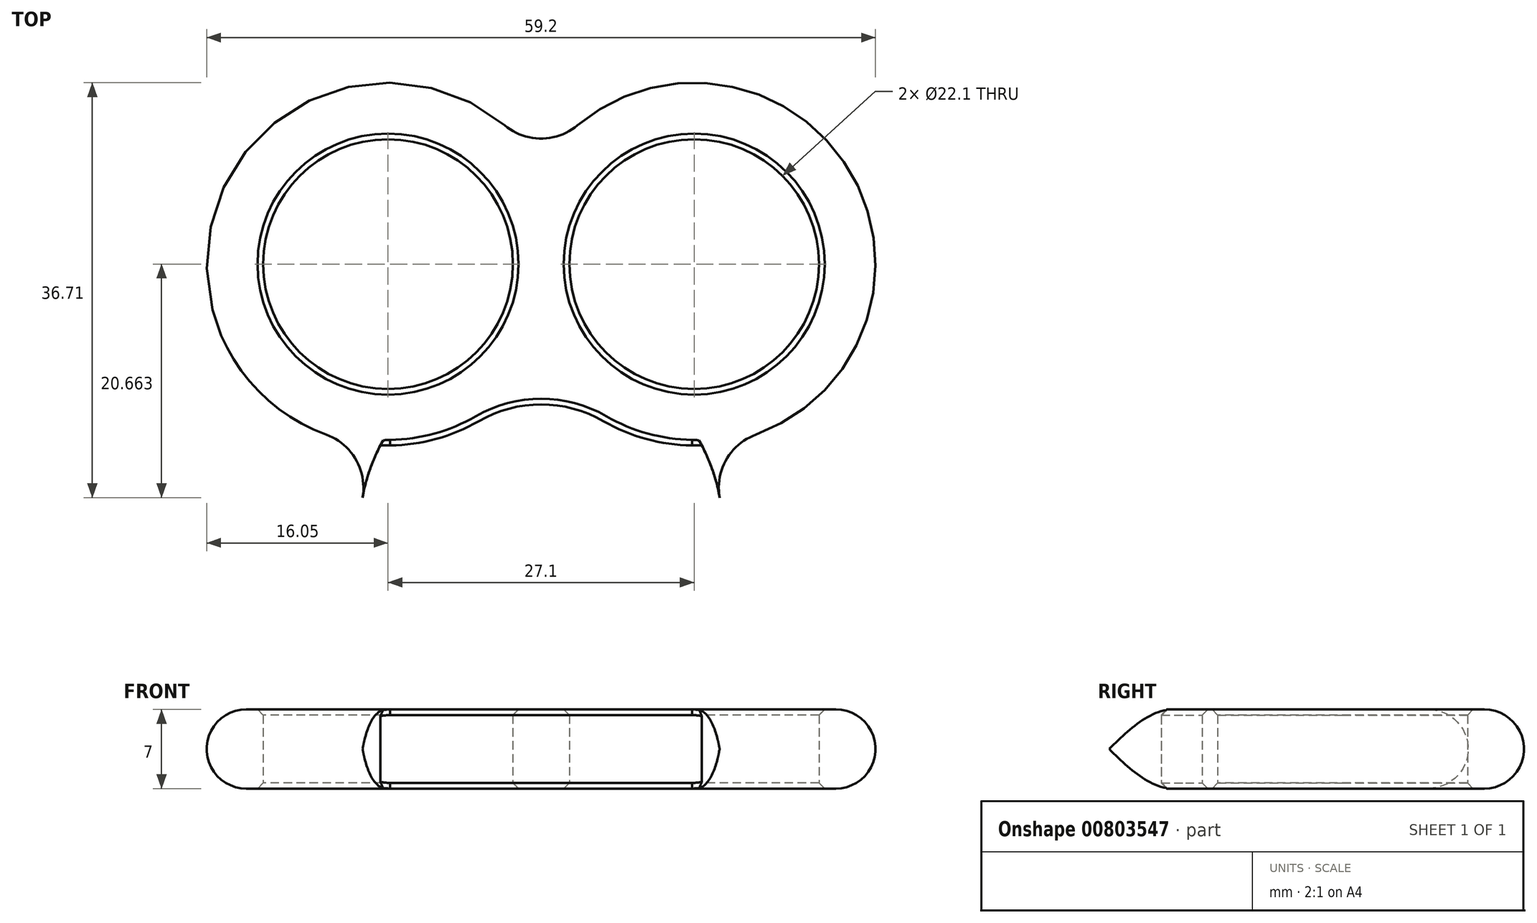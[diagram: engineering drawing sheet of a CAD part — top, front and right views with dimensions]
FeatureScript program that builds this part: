
annotation { "Feature Type Name" : "Feature", "Feature Type Description" : "" }
export const myFeature = defineFeature(function(context is Context, id is Id, definition is map)
    precondition{}
    {
        {
            var Q0;
            Q0=qCreatedBy(makeId("Top.planeOp"),FACE);
            var sketch = newSketch(context, id + "F0", { "sketchPlane" : qUnion([Q0])});
            skCircle(sketch, "E0", {"center": v(-13.55, 7.82) * mm, "radius": 11.05 * mm});
            skCircle(sketch, "E1", {"center": v(13.55, 7.82) * mm, "radius": 11.05 * mm});
            skCircle(sketch, "E2", {"center": v(0, -15.65) * mm, "radius": 11.05 * mm});
            skLineSegment(sketch, "E3", {"start": v(-13.55, 7.82) * mm, "end": v(13.55, 7.82) * mm, "construction": true});
            skLineSegment(sketch, "E4", {"start": v(13.55, 7.82) * mm, "end": v(0, -15.65) * mm, "construction": true});
            skLineSegment(sketch, "E5", {"start": v(0, -15.65) * mm, "end": v(-13.55, 7.82) * mm, "construction": true});
            skLineSegment(sketch, "E6", {"start": v(6.77, -3.91) * mm, "end": v(-13.55, 7.82) * mm, "construction": true});
            skArc(sketch, "E7", {"start": v(-3.22, 20.1) * mm, "mid": v(-27.45, 15.85) * mm, "end": v(-19.02, -7.27) * mm});
            skArc(sketch, "E8", {"start": v(19.02, -7.27) * mm, "mid": v(27.45, 15.85) * mm, "end": v(3.22, 20.1) * mm});
            skArc(sketch, "E9", {"start": v(-0.67, 0.39) * mm, "mid": v(0, -31.7) * mm, "end": v(0.67, 0.39) * mm});
            skArc(sketch, "E10.trimOffspring", {"start": v(0, -0.78) * mm, "mid": v(27.45, 15.85) * mm, "end": v(-0.67, 0.39) * mm});
            skArc(sketch, "E11.trimOffspring", {"start": v(-15.8, -12.84) * mm, "mid": v(0, -31.7) * mm, "end": v(15.8, -12.84) * mm});
            skArc(sketch, "E12.trimOffspring", {"start": v(0.67, 0.39) * mm, "mid": v(-27.45, 15.85) * mm, "end": v(0, -0.78) * mm});
            skPoint(sketch, "E13.visualSharp", {"position": v(0, 16.43) * mm});
            skArc(sketch, "E13.filletArc", {"start": v(-3.22, 20.1) * mm, "mid": v(0, 18.93) * mm, "end": v(3.22, 20.1) * mm});
            skPoint(sketch, "E14.visualSharp", {"position": v(14.22, -8.21) * mm});
            skArc(sketch, "E14.filletArc", {"start": v(19.02, -7.27) * mm, "mid": v(16.4, -9.47) * mm, "end": v(15.8, -12.84) * mm});
            skPoint(sketch, "E15.visualSharp", {"position": v(-14.22, -8.21) * mm});
            skArc(sketch, "E15.filletArc", {"start": v(-15.8, -12.84) * mm, "mid": v(-16.4, -9.47) * mm, "end": v(-19.02, -7.27) * mm});
            skSolve(sketch);
        }
        {
            var Q0;
            Q0=makeQuery(id+"F0.imprint","IMPRINT",FACE,{"disambiguationData":[TD([[makeQuery(id+"F0.imprint","IMPRINT",EDGE,{"derivedFrom":sQuery(id+"F0.wireOp",EDGE,"E0")}),-1.0]])]});
            var Q1;
            {var subQ4=sQuery(id+"F0.wireOp",EDGE,"E9");var subQ5=sQuery(id+"F0.wireOp",EDGE,"E0");var subQ6=makeQuery(id+"F0.imprint","INTERSECT",VERTEX,{"derivedFrom":[subQ5,subQ4]});Q1=makeQuery(id+"F0.imprint","IMPRINT",FACE,{"disambiguationData":[TD([[makeQuery(id+"F0.imprint","IMPRINT",EDGE,{"disambiguationData":[TD([[subQ6,1.0]])],"derivedFrom":subQ5}),-1.0]])]});}
            var Q2;
            {var subQ1=sQuery(id+"F0.wireOp",EDGE,"E9");var subQ5=sQuery(id+"F0.wireOp",EDGE,"E10.trimOffspring");var subQ13=makeQuery(id+"F0.imprint","INTERSECT",VERTEX,{"disambiguationData":[OD(0.0)],"derivedFrom":[subQ1,subQ5]});Q2=makeQuery(id+"F0.imprint","IMPRINT",FACE,{"disambiguationData":[TD([[makeQuery(id+"F0.imprint","IMPRINT",EDGE,{"disambiguationData":[TD([[subQ13,-1.0]])],"derivedFrom":subQ1}),1.0]])]});}
            var Q3;
            {var subQ2=sQuery(id+"F0.wireOp",EDGE,"E9");var subQ4=sQuery(id+"F0.wireOp",EDGE,"E1");var subQ5=makeQuery(id+"F0.imprint","INTERSECT",VERTEX,{"derivedFrom":[subQ4,subQ2]});Q3=makeQuery(id+"F0.imprint","IMPRINT",FACE,{"disambiguationData":[TD([[makeQuery(id+"F0.imprint","IMPRINT",EDGE,{"disambiguationData":[TD([[subQ5,-1.0]])],"derivedFrom":subQ4}),-1.0]])]});}
            var Q4;
            {var subQ0=sQuery(id+"F0.wireOp",EDGE,"E13.filletArc");Q4=makeQuery(id+"F0.imprint","IMPRINT",FACE,{"disambiguationData":[TD([[makeQuery(id+"F0.imprint","IMPRINT",EDGE,{"derivedFrom":subQ0}),-1.0]])]});}
            var Q5;
            {var subQ0=sQuery(id+"F0.wireOp",EDGE,"E14.filletArc");Q5=makeQuery(id+"F0.imprint","IMPRINT",FACE,{"disambiguationData":[TD([[makeQuery(id+"F0.imprint","IMPRINT",EDGE,{"derivedFrom":subQ0}),-1.0]])]});}
            var Q6;
            {var subQ0=sQuery(id+"F0.wireOp",EDGE,"E11.trimOffspring");Q6=makeQuery(id+"F0.imprint","IMPRINT",FACE,{"disambiguationData":[TD([[makeQuery(id+"F0.imprint","IMPRINT",EDGE,{"derivedFrom":subQ0}),1.0]])]});}
            var Q7;
            {var subQ0=sQuery(id+"F0.wireOp",EDGE,"E10.trimOffspring");var subQ1=sQuery(id+"F0.wireOp",EDGE,"E2");var subQ2=makeQuery(id+"F0.imprint","INTERSECT",VERTEX,{"derivedFrom":[subQ1,subQ0]});Q7=makeQuery(id+"F0.imprint","IMPRINT",FACE,{"disambiguationData":[TD([[makeQuery(id+"F0.imprint","IMPRINT",EDGE,{"disambiguationData":[TD([[subQ2,-1.0]])],"derivedFrom":subQ1}),-1.0]])]});}
            var Q8;
            {var subQ0=sQuery(id+"F0.wireOp",EDGE,"E15.filletArc");Q8=makeQuery(id+"F0.imprint","IMPRINT",FACE,{"disambiguationData":[TD([[makeQuery(id+"F0.imprint","IMPRINT",EDGE,{"derivedFrom":subQ0}),-1.0]])]});}
            var Q9;
            {var subQ0=sQuery(id+"F0.wireOp",EDGE,"E9");var subQ1=sQuery(id+"F0.wireOp",EDGE,"E1");var subQ2=makeQuery(id+"F0.imprint","INTERSECT",VERTEX,{"derivedFrom":[subQ1,subQ0]});Q9=makeQuery(id+"F0.imprint","IMPRINT",FACE,{"disambiguationData":[TD([[makeQuery(id+"F0.imprint","IMPRINT",EDGE,{"disambiguationData":[TD([[subQ2,1.0]])],"derivedFrom":subQ1}),-1.0]])]});}
            extrude(context, id + "F1", {"entities" : qUnion([Q0, Q1, Q2, Q3, Q4, Q5, Q6, Q7, Q8, Q9]), "depth" : 7 * mm, "offsetDistance" : 25 * mm});
        }
        {
            var Q0;
            Q0=makeQuery(id+"F1.opExtrude","CAP_EDGE",EDGE,{"disambiguationData":[OSD([sQuery(id+"F0.wireOp",EDGE,"E14.filletArc")])],"isStart":false});
            var Q1;
            Q1=makeQuery(id+"F1.opExtrude","CAP_EDGE",EDGE,{"disambiguationData":[OSD([sQuery(id+"F0.wireOp",EDGE,"E14.filletArc")])],"isStart":true});
            fillet(context, id + "F2", {"entities" : qUnion([Q0, Q1]), "radius" : 3.5 * mm, "tangentPropagation" : true, "allowEdgeOverflow" : false});
        }
        {
            var Q0;
            Q0=makeQuery(id+"F1.opExtrude","CAP_EDGE",EDGE,{"disambiguationData":[OSD([sQuery(id+"F0.wireOp",EDGE,"E1")])],"isStart":false});
            var Q1;
            Q1=makeQuery(id+"F1.opExtrude","CAP_EDGE",EDGE,{"disambiguationData":[OSD([sQuery(id+"F0.wireOp",EDGE,"E1")])],"isStart":true});
            var Q2;
            Q2=makeQuery(id+"F1.opExtrude","CAP_EDGE",EDGE,{"disambiguationData":[OSD([sQuery(id+"F0.wireOp",EDGE,"E0")])],"isStart":true});
            var Q3;
            Q3=makeQuery(id+"F1.opExtrude","CAP_EDGE",EDGE,{"disambiguationData":[OSD([sQuery(id+"F0.wireOp",EDGE,"E0")])],"isStart":false});
            var Q4;
            Q4=makeQuery(id+"F1.opExtrude","CAP_EDGE",EDGE,{"disambiguationData":[OSD([sQuery(id+"F0.wireOp",EDGE,"E2")])],"isStart":false});
            var Q5;
            Q5=makeQuery(id+"F1.opExtrude","CAP_EDGE",EDGE,{"disambiguationData":[OSD([sQuery(id+"F0.wireOp",EDGE,"E2")])],"isStart":true});
            chamfer(context, id + "F3", {"entities" : qUnion([Q0, Q1, Q2, Q3, Q4, Q5]), "width" : .5 * mm, "tangentPropagation" : true});
        }
    });
